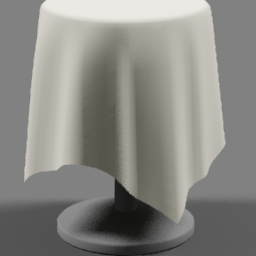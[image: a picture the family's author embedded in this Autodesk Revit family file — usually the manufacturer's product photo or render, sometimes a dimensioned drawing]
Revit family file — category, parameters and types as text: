
# Revit family: Layout-Teknion-Aarea_Small_Conversation_01-R2022
name_source: partatom
category: Furniture Systems
units: mm (PartAtom-declared; Revit-internal decimal feet)

## family parameters
Always vertical = Yes
Cut with Voids When Loaded = No
OmniClass Number = 23.40.70.14.64.21
OmniClass Title = Systems Furniture
Part Type = Normal
Room Calculation Point = No
Round Connector Dimension = Use Diameter
Shared = Yes
Work Plane-Based = No

## types (1)
- Aarea Small Conversation 01
    Assembly Code = E2020200
    Default Elevation = 0' - 0"
    Description = 10'-0" x 10'-0" Overall
    Manufacturer = Teknion
    Manufacturer Fax = 416.661.4586
    Model = Aarea Small Conversation 01
    Product Line = Aarea
    Product Page URL = https://www.teknionplanningtool.com
    Series = Aarea
    Sustainability Data = https://www.teknion.com
    URL = www.teknion.com
    Unit Weight URL = http://www.teknion.com
    Warranty = http://www.teknion.com

## geometry (parser evidence)
native form markers: Blend x15, Sweep x16
no freeform markers — native parametric forms only
